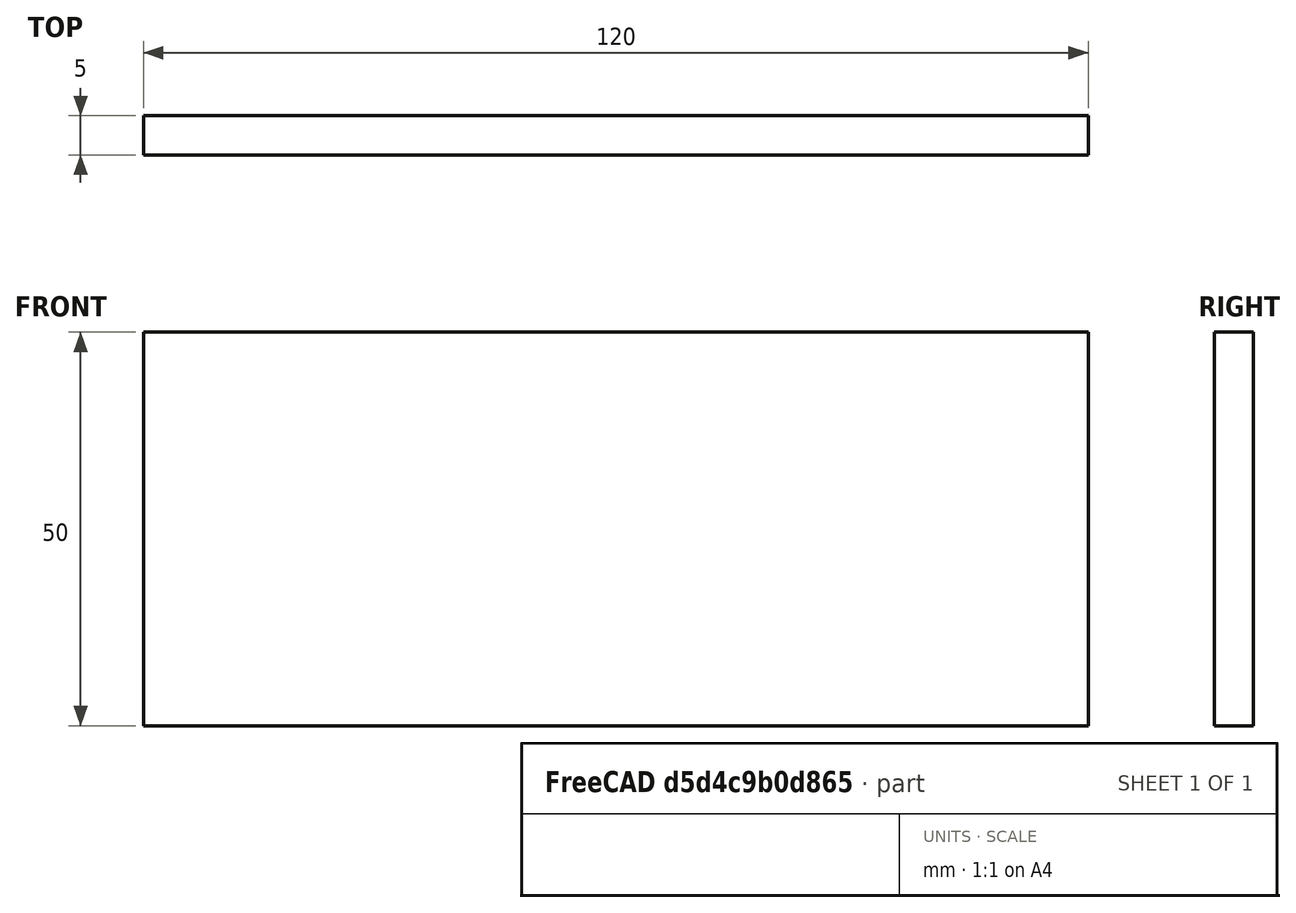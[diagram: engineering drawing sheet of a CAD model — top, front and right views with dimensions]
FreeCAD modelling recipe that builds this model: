
FCSTD DOCUMENT  (FreeCAD 0.15R4671 (Git))
Label: Flat Bar 120x5 EN10058 S235JR
License: All rights reserved
LicenseURL: http://en.wikipedia.org/wiki/All_rights_reserved
objects: Sketcher::SketchObject×1, Part::Extrusion×1
note: 2 computed .brp shape members not serialized (recipe doc carries the construction recipe); baked Part::Feature solids carry a one-line shape summary decoded from their .brp

FEATURE [Sketcher::SketchObject] Sketch
  sketch-geometry (4):
    g0: LineSegment StartX=-60 StartY=-2.5 StartZ=0 EndX=60 EndY=-2.5 EndZ=0
    g1: LineSegment StartX=60 StartY=-2.5 StartZ=0 EndX=60 EndY=2.5 EndZ=0
    g2: LineSegment StartX=60 StartY=2.5 StartZ=0 EndX=-60 EndY=2.5 EndZ=0
    g3: LineSegment StartX=-60 StartY=2.5 StartZ=0 EndX=-60 EndY=-2.5 EndZ=0
  constraints (12):
    c: Coincident(g0,g1)
    c: Coincident(g1,g2)
    c: Coincident(g2,g3)
    c: Coincident(g3,g0)
    c: Horizontal(g0)
    c: Horizontal(g2)
    c: Vertical(g1)
    c: Vertical(g3)
    c: Symmetric(g1,g2,g-2)
    c: Symmetric(g0,g1,g-1)
    c: DistanceY(g1) = 5
    c: DistanceX(g0) = 120
FEATURE [Part::Extrusion] Extrude  label="Flat Bar 120x5 EN10058 S235JR"
  Base = -> Sketch
  Dir = (0,0,50)
  Solid = true
